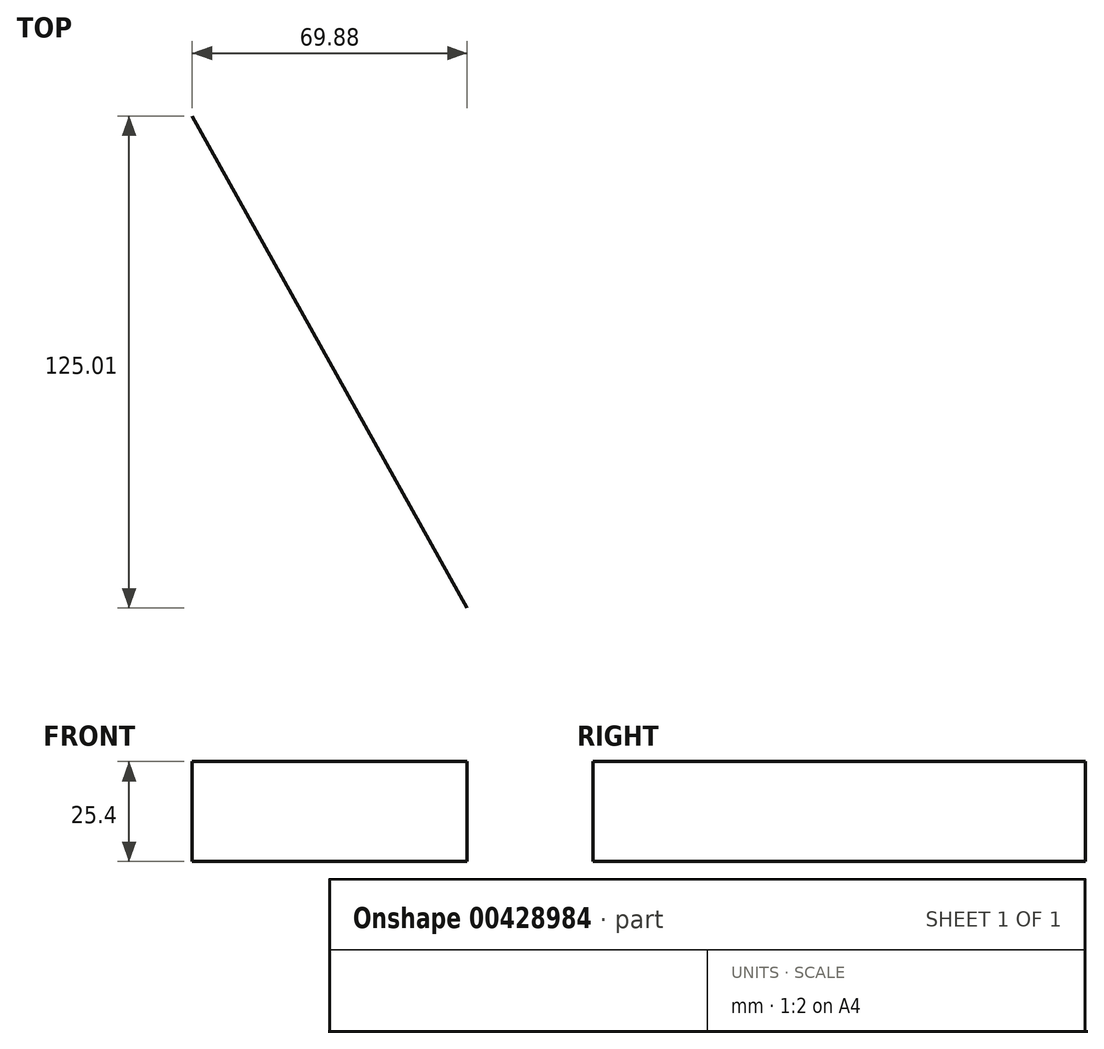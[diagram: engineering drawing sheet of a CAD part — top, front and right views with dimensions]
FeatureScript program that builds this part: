
annotation { "Feature Type Name" : "Feature", "Feature Type Description" : "" }
export const myFeature = defineFeature(function(context is Context, id is Id, definition is map)
    precondition{}
    {
        {
            var Q0;
            Q0=qCreatedBy(makeId("Top.planeOp"),FACE);
            var sketch = newSketch(context, id + "F0", { "sketchPlane" : qUnion([Q0])});
            skLineSegment(sketch, "E0", {"start": v(87.88, -156.65) * mm, "end": v(0, 0) * mm});
            skLineSegment(sketch, "E1", {"start": v(0, 0) * mm, "end": v(81.67, 0) * mm});
            skLineSegment(sketch, "E2", {"start": v(81.67, 0) * mm, "end": v(151.55, -125.01) * mm});
            skLineSegment(sketch, "E3", {"start": v(151.55, -125.01) * mm, "end": v(87.88, -156.65) * mm});
            skSolve(sketch);
        }
        {
            var Q0;
            Q0=sQuery(id+"F0.wireOp",EDGE,"E2");
            extrude(context, id + "F1", {"bodyType" : ToolBodyType.SURFACE, "surfaceEntities" : qUnion([Q0]), "depth" : 25.4 * mm});
        }
    });
